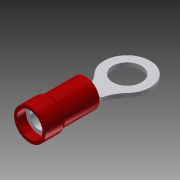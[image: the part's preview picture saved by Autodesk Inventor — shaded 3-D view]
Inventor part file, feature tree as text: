
AUTODESK INVENTOR PART (.ipt)
format: ipt  version: 2014 (Build 180170000, 170)  size: 409,088 bytes
history: native  units: in
note: dims shown in document units (in); Inventor stores cm internally (conversion verified against a paired STEP export)
features: sketch x6, projected_geometry x5, extrude x4, fillet x4, shell x1, revolve x1, plane x1, loft x1, chamfer x1, other x1
ambient origin geometry x8: Origin, YZ Plane, XZ Plane, XY Plane, X Axis, Y Axis, Z Axis, Center Point
bodies: Solid1 (feature_tree), Solid2 (feature_tree)
feature tree (25):
  extrude  "Extrusion1"  Depth=0.38in TaperAngle=0.0deg
  extrude  "Extrusion2"  Depth=0.03in TaperAngle=0.0deg
  fillet  "Fillet1"  Radius=0.01in
  fillet  "Fillet2"  Radius=0.03in
  shell  "Shell1"  Thickness=0.02in
  revolve  "Revolution1"  [1 undecoded]
  plane  "Work Plane1"
  extrude  "Extrusion3"  TaperAngle=90.0deg  [1 undecoded]
  loft  "Loft1"
  fillet  "Fillet3"  Radius=0.315in
  fillet  "Fillet4"  Radius=0.06in
  extrude  "Extrusion4"  Depth=0.0275in TaperAngle=0.0deg
  chamfer  "Chamfer1"  Angle=90.0deg  [1 undecoded]
  sketch  "Sketch1"  dims[d0=0.1895in d1=0.38in d2=0.0in]
  sketch  "Sketch2"  dims[d3=0.2135in d4=0.136in d5=0.0in d6=0.01in d7=0.03in d8=0.02in]
  projected_geometry  "Projected Loop1"
  sketch  "Sketch3"  dims[d9=0.028in d10=0.028in]
  sketch  "Sketch4"  dims[d11=0.058in d12=90.0deg]
  sketch  "Sketch5"  dims[d13=-0.06in d14=0.283in d15=0.315in d16=0.06in]
  projected_geometry  "Projected Loop2"
  other  "Edges1"
  sketch  "Sketch6"  dims[d17=0.06in d18=0.0275in d19=0.0in d20=0.0in d21=90.0deg d22=0.0in d23=90.0deg d24=0.03in d25=0.03in d26=0.005in d27=0.0275in d28=0.0in d29=0.003in d30=0.125in d31=45.0deg]
  projected_geometry  "Projected Loop3"
  projected_geometry  "Project Cut Edges1"
  projected_geometry  "Project Cut Edges2"
note: 3 required parameter values undecoded (feature->parameter linkage not recoverable at this tier; creation-order binding heuristic only, values carry confidence <= 0.55)